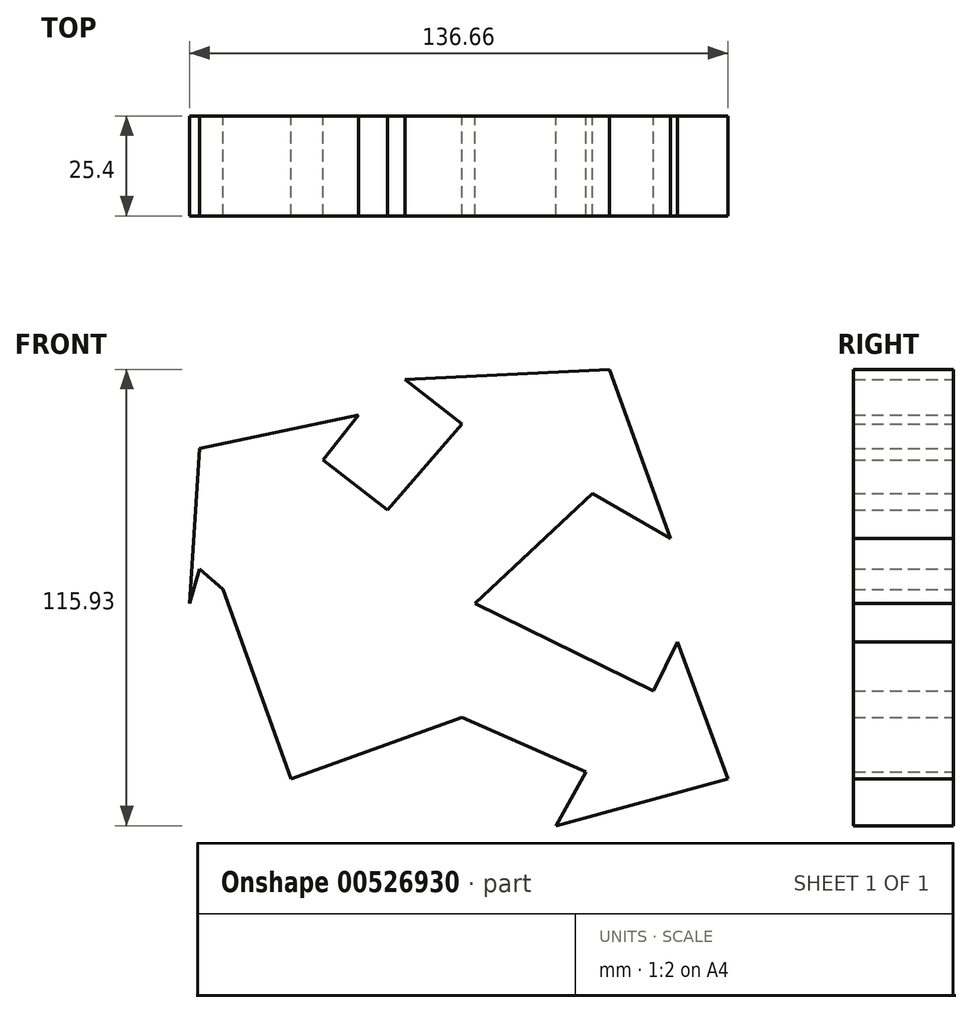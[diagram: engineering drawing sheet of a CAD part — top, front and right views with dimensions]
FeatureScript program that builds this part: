
annotation { "Feature Type Name" : "Feature", "Feature Type Description" : "" }
export const myFeature = defineFeature(function(context is Context, id is Id, definition is map)
    precondition{}
    {
        {
            var Q0;
            Q0=qCreatedBy(makeId("Front.planeOp"),FACE);
            var sketch = newSketch(context, id + "F0", { "sketchPlane" : qUnion([Q0])});
            skLineSegment(sketch, "E0", {"start": v(0, 0) * mm, "end": v(-22.2, 23.75) * mm});
            skLineSegment(sketch, "E1", {"start": v(-22.2, 23.75) * mm, "end": v(-51, -8.18) * mm});
            skLineSegment(sketch, "E2", {"start": v(-51, -8.18) * mm, "end": v(-63.95, 3.5) * mm});
            skLineSegment(sketch, "E3", {"start": v(-63.95, 3.5) * mm, "end": v(-46.72, -44.58) * mm});
            skLineSegment(sketch, "E4", {"start": v(-46.72, -44.58) * mm, "end": v(-3.21, -29) * mm});
            skLineSegment(sketch, "E5", {"start": v(-3.21, -29) * mm, "end": v(-24.92, -24.53) * mm});
            skLineSegment(sketch, "E6", {"start": v(-24.92, -24.53) * mm, "end": v(0, 0) * mm});
            skLineSegment(sketch, "E7", {"start": v(-22.2, 23.75) * mm, "end": v(-3.21, 45.55) * mm});
            skLineSegment(sketch, "E8", {"start": v(0, 0) * mm, "end": v(29.91, 27.95) * mm});
            skLineSegment(sketch, "E9", {"start": v(29.91, 27.95) * mm, "end": v(49.64, 16.55) * mm});
            skLineSegment(sketch, "E10", {"start": v(49.64, 16.55) * mm, "end": v(34.26, 59.48) * mm});
            skLineSegment(sketch, "E11", {"start": v(34.26, 59.48) * mm, "end": v(-17.72, 56.84) * mm});
            skLineSegment(sketch, "E12", {"start": v(-17.72, 56.84) * mm, "end": v(-3.21, 45.55) * mm});
            skLineSegment(sketch, "E13", {"start": v(0, 0) * mm, "end": v(45.36, -22.2) * mm});
            skLineSegment(sketch, "E14", {"start": v(-3.21, -29) * mm, "end": v(28.23, -42.83) * mm});
            skLineSegment(sketch, "E15", {"start": v(28.23, -42.83) * mm, "end": v(20.64, -56.45) * mm});
            skLineSegment(sketch, "E16", {"start": v(20.64, -56.45) * mm, "end": v(64.24, -44.58) * mm});
            skLineSegment(sketch, "E17", {"start": v(45.36, -22.2) * mm, "end": v(51.44, -9.76) * mm});
            skLineSegment(sketch, "E18", {"start": v(51.44, -9.76) * mm, "end": v(64.24, -44.58) * mm});
            skLineSegment(sketch, "E19", {"start": v(-22.2, 23.75) * mm, "end": v(-38.53, 36.47) * mm});
            skLineSegment(sketch, "E20", {"start": v(-38.53, 36.47) * mm, "end": v(-29.61, 47.93) * mm});
            skLineSegment(sketch, "E21", {"start": v(-63.95, 3.5) * mm, "end": v(-69.95, 8.73) * mm});
            skLineSegment(sketch, "E22", {"start": v(-69.95, 8.73) * mm, "end": v(-72.42, 0) * mm});
            skLineSegment(sketch, "E23", {"start": v(-72.42, 0) * mm, "end": v(-69.95, 39.32) * mm});
            skLineSegment(sketch, "E24", {"start": v(-69.95, 39.32) * mm, "end": v(-29.61, 47.93) * mm});
            skSolve(sketch);
        }
        {
            var Q0;
            Q0=makeQuery(id+"F0.imprint","IMPRINT",FACE,{"disambiguationData":[TD([[makeQuery(id+"F0.imprint","IMPRINT",EDGE,{"derivedFrom":sQuery(id+"F0.wireOp",EDGE,"E0")}),-1.0]])]});
            var Q1;
            Q1=makeQuery(id+"F0.imprint","IMPRINT",FACE,{"disambiguationData":[TD([[makeQuery(id+"F0.imprint","IMPRINT",EDGE,{"derivedFrom":sQuery(id+"F0.wireOp",EDGE,"E1")}),-1.0]])]});
            var Q2;
            Q2=makeQuery(id+"F0.imprint","IMPRINT",FACE,{"disambiguationData":[TD([[makeQuery(id+"F0.imprint","IMPRINT",EDGE,{"derivedFrom":sQuery(id+"F0.wireOp",EDGE,"E0")}),1.0]])]});
            var Q3;
            Q3=makeQuery(id+"F0.imprint","IMPRINT",FACE,{"disambiguationData":[TD([[makeQuery(id+"F0.imprint","IMPRINT",EDGE,{"derivedFrom":sQuery(id+"F0.wireOp",EDGE,"E5")}),-1.0]])]});
            extrude(context, id + "F1", {"entities" : qUnion([Q0, Q1, Q2, Q3]), "depth" : 25.4 * mm, "offsetDistance" : 25.4 * mm});
        }
    });
